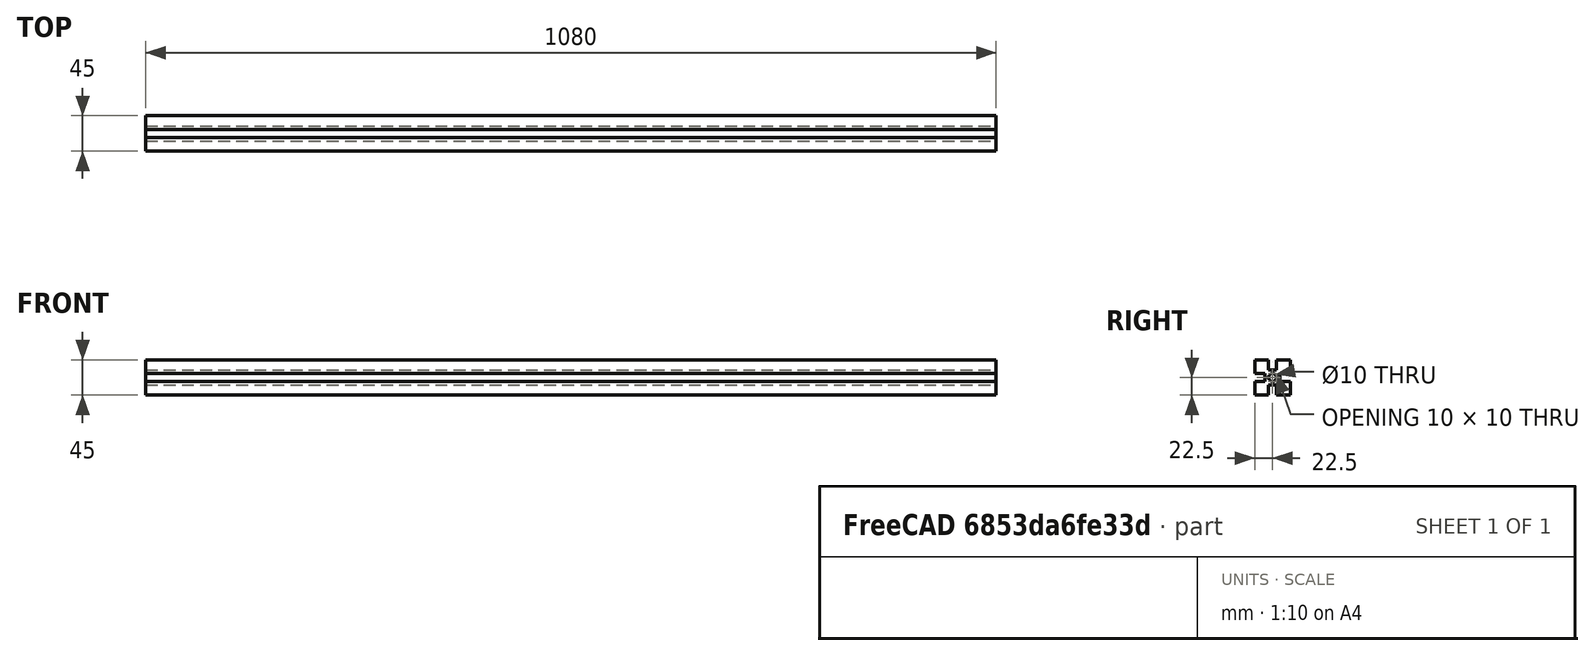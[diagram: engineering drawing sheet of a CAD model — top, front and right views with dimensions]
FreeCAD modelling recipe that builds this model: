
FCSTD DOCUMENT  (FreeCAD 1.0R39109 (Git))
Label: vslot 45x45x1080
License: All rights reserved
LicenseURL: https://en.wikipedia.org/wiki/All_rights_reserved
objects: Part::Feature×1, PartDesign::FeatureBase×1, PartDesign::Pad×1, PartDesign::Pocket×1, PartDesign::Body×1
note: 10 computed .brp shape members not serialized (recipe doc carries the construction recipe); baked Part::Feature solids carry a one-line shape summary decoded from their .brp

FEATURE [Part::Feature] Part__Feature  label="1"
  shape: bbox 1000 x 45 x 45 mm, 24 faces (baked)
FEATURE [PartDesign::FeatureBase] BaseFeature
  BaseFeature = -> Part__Feature
  Suppressed = false
FEATURE [PartDesign::Pad] Pad
  BaseFeature = -> BaseFeature
  Direction = (1,0,0)
  Length = 220
  Length2 = 10
  Profile = -> BaseFeature [Face24]
  Refine = true
  Suppressed = false
  Type = 0
FEATURE [PartDesign::Pocket] Pocket
  BaseFeature = -> Pad
  Direction = (-1,0,0)
  Length = 140
  Length2 = 5
  Profile = -> Pad [Face3]
  Refine = true
  Suppressed = false
  Type = 0
FEATURE [PartDesign::Body] Body
  AllowCompound = false
  BaseFeature = -> Part__Feature
  Group = -> [BaseFeature,Pad,Pocket]
  Origin = -> Origin
  Tip = -> Pocket
